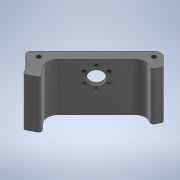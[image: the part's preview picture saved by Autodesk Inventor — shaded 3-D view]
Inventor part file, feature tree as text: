
AUTODESK INVENTOR PART (.ipt)
format: ipt  version: 2020 (Build 240168000, 168)  size: 582,144 bytes
history: native  units: mm
features: extrude x4, sketch x3, other x1, chamfer x1, fillet x1
ambient origin geometry x8: Origin, YZ Plane, XZ Plane, XY Plane, X Axis, Y Axis, Z Axis, Center Point
bodies: Body1 (feature_tree)
feature tree (10):
  other  "Твердое тело1"
  sketch  "Эскиз1"
  extrude  "Выдавливание10"  Depth=3.0mm
  sketch  "Эскиз6"
  extrude  "Выдавливание13"  Depth=6.0mm
  extrude  "Выдавливание14"  Depth=35.0mm TaperAngle=0.0deg
  chamfer  "Фаска3"  Distance=59.0mm
  extrude  "Выдавливание15"  Depth=21.2mm
  fillet  "Сопряжение1"  Radius=15.0mm
  sketch  "Эскиз7"
